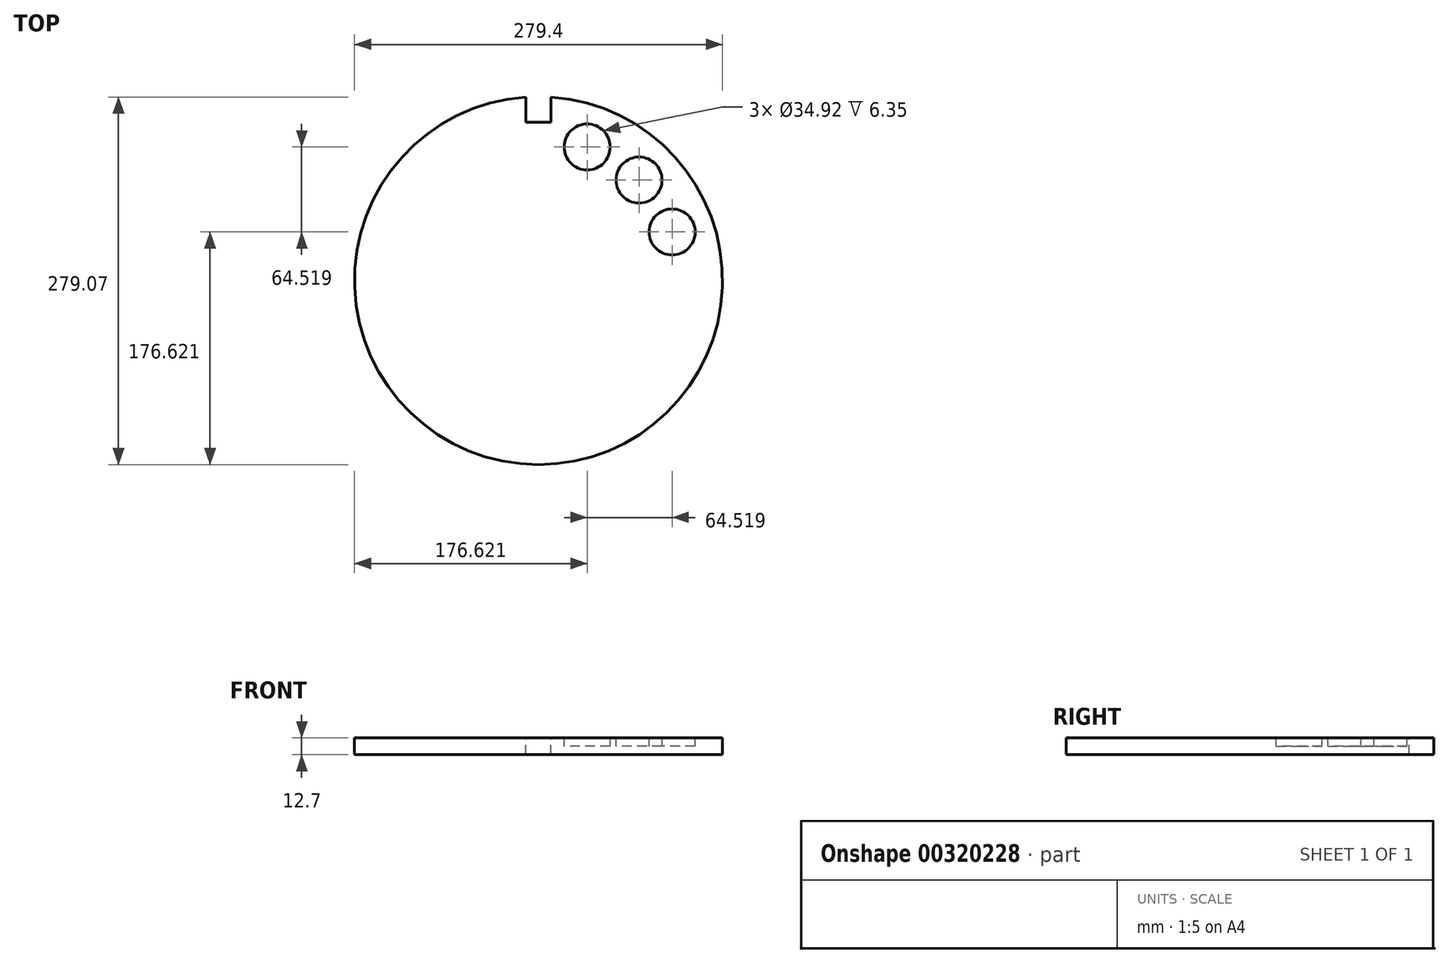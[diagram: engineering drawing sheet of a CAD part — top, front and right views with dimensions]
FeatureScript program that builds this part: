
annotation { "Feature Type Name" : "Feature", "Feature Type Description" : "" }
export const myFeature = defineFeature(function(context is Context, id is Id, definition is map)
    precondition{}
    {
        {
            var Q0;
            Q0=qCreatedBy(makeId("Top.planeOp"),FACE);
            var sketch = newSketch(context, id + "F0", { "sketchPlane" : qUnion([Q0])});
            skCircle(sketch, "E0", {"center": v(0, 0) * mm, "radius": 107.95 * mm, "construction": true});
            skCircle(sketch, "E1", {"center": v(0, 0) * mm, "radius": 139.7 * mm});
            skLineSegment(sketch, "E2", {"start": v(0, 0) * mm, "end": v(139.7, 0) * mm, "construction": true});
            skLineSegment(sketch, "E3", {"start": v(0, 0) * mm, "end": v(0, 139.7) * mm, "construction": true});
            skLineSegment(sketch, "E4", {"start": v(0, 0) * mm, "end": v(76.33, 76.33) * mm, "construction": true});
            skLineSegment(sketch, "E5", {"start": v(0, 0) * mm, "end": v(101.44, 36.92) * mm, "construction": true});
            skLineSegment(sketch, "E6", {"start": v(0, 0) * mm, "end": v(36.92, 101.44) * mm, "construction": true});
            skCircle(sketch, "E7", {"center": v(36.92, 101.44) * mm, "radius": 17.46 * mm});
            skCircle(sketch, "E8", {"center": v(76.33, 76.33) * mm, "radius": 17.46 * mm});
            skCircle(sketch, "E9", {"center": v(101.44, 36.92) * mm, "radius": 17.46 * mm});
            skLineSegment(sketch, "E10.top", {"start": v(-9.53, 113.97) * mm, "end": v(9.52, 113.97) * mm});
            skLineSegment(sketch, "E10.left", {"start": v(-9.53, 139.37) * mm, "end": v(-9.53, 113.97) * mm});
            skLineSegment(sketch, "E10.right", {"start": v(9.52, 139.37) * mm, "end": v(9.52, 113.97) * mm});
            skPoint(sketch, "E10.middle", {"position": v(0, 126.67) * mm});
            skLineSegment(sketch, "E11", {"start": v(-9.53, 120.32) * mm, "end": v(9.52, 120.32) * mm});
            skCircle(sketch, "E12", {"center": v(0, 0) * mm, "radius": 44.84 * mm});
            skSolve(sketch);
        }
        {
            var Q0;
            Q0=qSketchRegion(id+"F0",true);
            var Q1;
            Q1=makeQuery(id+"F0.imprint","IMPRINT",FACE,{"disambiguationData":[TD([[makeQuery(id+"F0.imprint","IMPRINT",EDGE,{"derivedFrom":sQuery(id+"F0.wireOp",EDGE,"E7")}),1.0]])]});
            var Q2;
            Q2=makeQuery(id+"F0.imprint","IMPRINT",FACE,{"disambiguationData":[TD([[makeQuery(id+"F0.imprint","IMPRINT",EDGE,{"derivedFrom":sQuery(id+"F0.wireOp",EDGE,"E8")}),1.0]])]});
            var Q3;
            Q3=makeQuery(id+"F0.imprint","IMPRINT",FACE,{"disambiguationData":[TD([[makeQuery(id+"F0.imprint","IMPRINT",EDGE,{"derivedFrom":sQuery(id+"F0.wireOp",EDGE,"E9")}),1.0]])]});
            var Q4;
            {var subQ0=sQuery(id+"F0.wireOp",EDGE,"E10.top");Q4=makeQuery(id+"F0.imprint","IMPRINT",FACE,{"disambiguationData":[TD([[makeQuery(id+"F0.imprint","IMPRINT",EDGE,{"derivedFrom":subQ0}),1.0]])]});}
            var Q5;
            Q5=makeQuery(id+"F0.imprint","IMPRINT",FACE,{"disambiguationData":[TD([[makeQuery(id+"F0.imprint","IMPRINT",EDGE,{"derivedFrom":sQuery(id+"F0.wireOp",EDGE,"E12")}),1.0]])]});
            extrude(context, id + "F1", {"entities" : qUnion([Q0, Q1, Q2, Q3, Q4, Q5]), "oppositeDirection" : true, "depth" : 12.7 * mm});
        }
        {
            var Q0;
            Q0=makeQuery(id+"F0.imprint","IMPRINT",FACE,{"disambiguationData":[TD([[makeQuery(id+"F0.imprint","IMPRINT",EDGE,{"derivedFrom":sQuery(id+"F0.wireOp",EDGE,"E7")}),1.0]])]});
            var Q1;
            Q1=makeQuery(id+"F0.imprint","IMPRINT",FACE,{"disambiguationData":[TD([[makeQuery(id+"F0.imprint","IMPRINT",EDGE,{"derivedFrom":sQuery(id+"F0.wireOp",EDGE,"E8")}),1.0]])]});
            var Q2;
            Q2=makeQuery(id+"F0.imprint","IMPRINT",FACE,{"disambiguationData":[TD([[makeQuery(id+"F0.imprint","IMPRINT",EDGE,{"derivedFrom":sQuery(id+"F0.wireOp",EDGE,"E9")}),1.0]])]});
            extrude(context, id + "F2", {"entities" : qUnion([Q0, Q1, Q2]), "operationType" : NewBodyOperationType.REMOVE, "oppositeDirection" : true, "depth" : 6.35 * mm});
        }
        {
            var Q0;
            {var subQ5=sQuery(id+"F0.wireOp",EDGE,"E11");Q0=makeQuery(id+"F0.imprint","IMPRINT",FACE,{"disambiguationData":[TD([[makeQuery(id+"F0.imprint","IMPRINT",EDGE,{"derivedFrom":subQ5}),1.0]])]});}
            extrude(context, id + "F3", {"entities" : qUnion([Q0]), "operationType" : NewBodyOperationType.REMOVE, "endBound" : BoundingType.THROUGH_ALL, "oppositeDirection" : true, "depth" : 25.4 * mm});
        }
        {
            var Q0;
            Q0=qCreatedBy(makeId("Front.planeOp"),FACE);
            var sketch = newSketch(context, id + "F4", { "sketchPlane" : qUnion([Q0])});
            skLineSegment(sketch, "E13", {"start": v(0, 0) * mm, "end": v(0, 89.72) * mm, "construction": true});
            skSolve(sketch);
        }
    });
